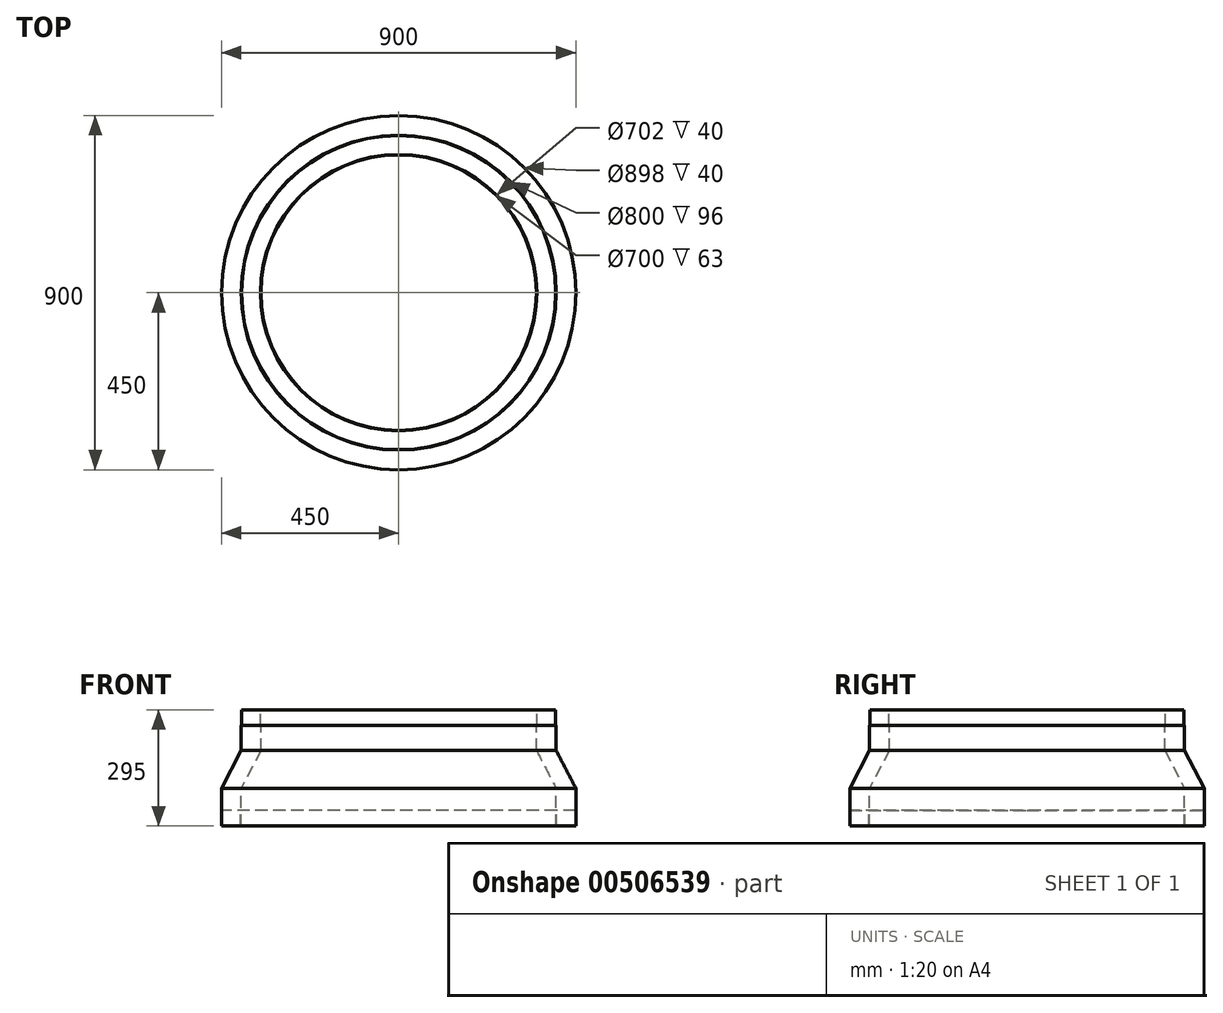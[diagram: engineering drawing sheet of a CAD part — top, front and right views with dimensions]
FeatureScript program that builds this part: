
annotation { "Feature Type Name" : "Feature", "Feature Type Description" : "" }
export const myFeature = defineFeature(function(context is Context, id is Id, definition is map)
    precondition{}
    {
        {
            var Q0;
            Q0=qCreatedBy(makeId("Front.planeOp"),FACE);
            var sketch = newSketch(context, id + "F0", { "sketchPlane" : qUnion([Q0])});
            skLineSegment(sketch, "E0", {"start": v(0, 433.08) * mm, "end": v(0, -434.74) * mm, "construction": true});
            skLineSegment(sketch, "E1", {"start": v(-400, -258.87) * mm, "end": v(-400, -162.87) * mm});
            skLineSegment(sketch, "E2", {"start": v(-400, -258.87) * mm, "end": v(-401, -258.87) * mm});
            skLineSegment(sketch, "E3", {"start": v(-401, -258.87) * mm, "end": v(-401, -218.87) * mm});
            skLineSegment(sketch, "E4", {"start": v(-401, -218.87) * mm, "end": v(-449, -218.87) * mm});
            skLineSegment(sketch, "E5", {"start": v(-449, -218.87) * mm, "end": v(-449, -258.87) * mm});
            skLineSegment(sketch, "E6", {"start": v(-449, -258.87) * mm, "end": v(-450, -258.87) * mm});
            skLineSegment(sketch, "E7", {"start": v(-450, -258.87) * mm, "end": v(-450, -162.87) * mm});
            skLineSegment(sketch, "E8", {"start": v(-399, 36.13) * mm, "end": v(-351, 36.13) * mm});
            skLineSegment(sketch, "E9", {"start": v(-351, 36.13) * mm, "end": v(-351, -3.87) * mm});
            skLineSegment(sketch, "E10", {"start": v(-351, -3.87) * mm, "end": v(-350, -3.87) * mm});
            skLineSegment(sketch, "E11", {"start": v(-350, -3.87) * mm, "end": v(-350, -66.87) * mm});
            skLineSegment(sketch, "E12", {"start": v(-399, 36.13) * mm, "end": v(-399, -3.87) * mm});
            skLineSegment(sketch, "E13", {"start": v(-399, -3.87) * mm, "end": v(-400, -3.87) * mm});
            skLineSegment(sketch, "E14", {"start": v(-400, -3.87) * mm, "end": v(-400, -66.87) * mm});
            skLineSegment(sketch, "E15", {"start": v(-350, -66.87) * mm, "end": v(-400, -162.87) * mm});
            skLineSegment(sketch, "E16", {"start": v(-400, -66.87) * mm, "end": v(-450, -162.87) * mm});
            skSolve(sketch);
        }
        {
            var Q0;
            Q0=qSketchRegion(id+"F0",true);
            var Q1;
            Q1=sQuery(id+"F0.wireOp",EDGE,"E0");
            revolve(context, id + "F1", {"entities" : qUnion([Q0]), "axis" : qUnion([Q1]), "revolveType" : RevolveType.FULL});
        }
    });
